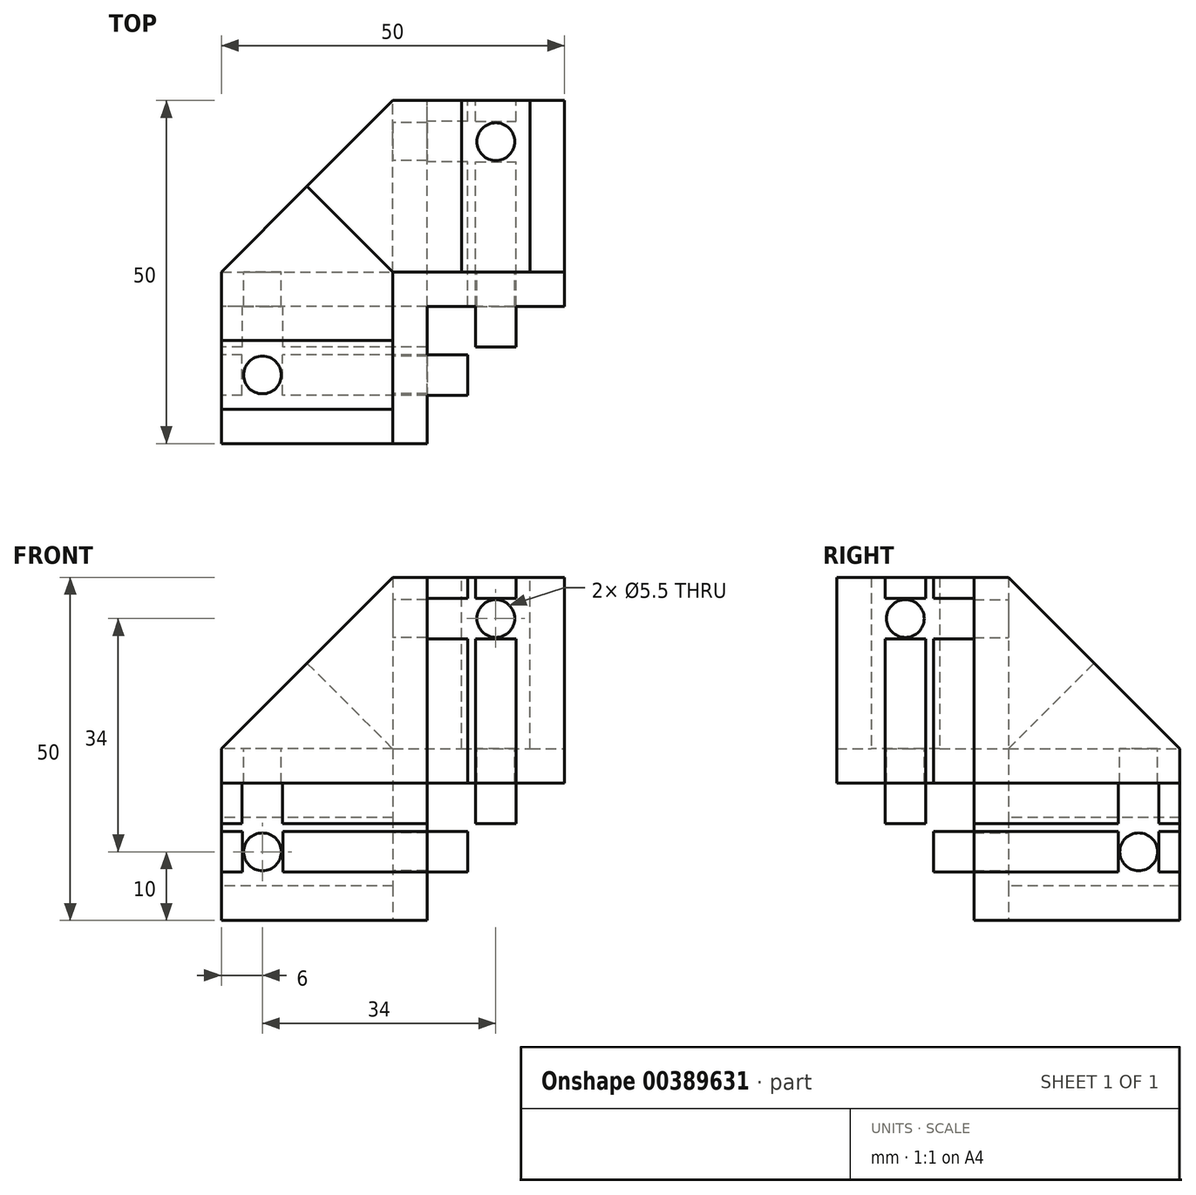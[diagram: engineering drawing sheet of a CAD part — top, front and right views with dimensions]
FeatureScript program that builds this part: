
annotation { "Feature Type Name" : "Feature", "Feature Type Description" : "" }
export const myFeature = defineFeature(function(context is Context, id is Id, definition is map)
    precondition{}
    {
        {
            var Q0;
            Q0=qCreatedBy(makeId("Top.planeOp"),FACE);
            var sketch = newSketch(context, id + "F0", { "sketchPlane" : qUnion([Q0])});
            skLineSegment(sketch, "E0", {"start": v(25, 25) * mm, "end": v(0, 25) * mm});
            skLineSegment(sketch, "E1", {"start": v(0, 25) * mm, "end": v(-25, 0) * mm});
            skLineSegment(sketch, "E2", {"start": v(-25, 0) * mm, "end": v(-25, -25) * mm});
            skLineSegment(sketch, "E3", {"start": v(-25, -25) * mm, "end": v(5, -25) * mm});
            skLineSegment(sketch, "E4", {"start": v(5, -25) * mm, "end": v(5, -5) * mm});
            skLineSegment(sketch, "E5", {"start": v(5, -5) * mm, "end": v(25, -5) * mm});
            skLineSegment(sketch, "E6", {"start": v(25, 25) * mm, "end": v(25, -5) * mm});
            skLineSegment(sketch, "E7", {"start": v(5, -5) * mm, "end": v(-25, -5) * mm});
            skLineSegment(sketch, "E8", {"start": v(5, -5) * mm, "end": v(5, 25) * mm});
            skSolve(sketch);
        }
        {
            var Q0;
            Q0=qSketchRegion(id+"F0",true);
            extrude(context, id + "F1", {"entities" : qUnion([Q0]), "depth" : 50 * mm});
        }
        {
            var Q0;
            {var subQ0=sQuery(id+"F0.wireOp",EDGE,"E3");Q0=makeQuery(id+"F0.imprint","IMPRINT",FACE,{"disambiguationData":[TD([[makeQuery(id+"F0.imprint","IMPRINT",EDGE,{"derivedFrom":subQ0}),1.0]])]});}
            var Q1;
            Q1=makeQuery(id+"F0.imprint","IMPRINT",FACE,{"disambiguationData":[TD([[makeQuery(id+"F0.imprint","IMPRINT",EDGE,{"derivedFrom":sQuery(id+"F0.wireOp",EDGE,"E5")}),1.0]])]});
            extrude(context, id + "F2", {"entities" : qUnion([Q0, Q1]), "operationType" : NewBodyOperationType.REMOVE, "depth" : 20 * mm});
        }
        {
            var Q0;
            Q0=makeQuery(id+"F1.opExtrude","CAP_EDGE",EDGE,{"disambiguationData":[OSD([sQuery(id+"F0.wireOp",EDGE,"E0")])],"isStart":false});
            var Q1;
            Q1=makeQuery(id+"F1.opExtrude","CAP_EDGE",EDGE,{"disambiguationData":[OSD([sQuery(id+"F0.wireOp",EDGE,"E2")])],"isStart":false});
            chamfer(context, id + "F3", {"entities" : qUnion([Q0, Q1]), "width" : 25 * mm, "tangentPropagation" : true});
        }
        {
            var Q0;
            Q0=makeQuery(id+"F1.opExtrude","SWEPT_FACE",FACE,{"disambiguationData":[OSD([sQuery(id+"F0.wireOp",EDGE,"E6")])]});
            cPlane(context, id + "F4", {"entities" : qUnion([Q0]), "cplaneType" : CPlaneType.OFFSET, "offset" : 5 * mm, "oppositeDirection" : true, "width" : 150 * mm, "height" : 150 * mm});
        }
        {
            var Q0;
            Q0=qCreatedBy(id+"F4.planeOp",FACE);
            var sketch = newSketch(context, id + "F5", { "sketchPlane" : qUnion([Q0])});
            skLineSegment(sketch, "E9.0", {"start": v(25, 25) * mm, "end": v(0, 50) * mm});
            skLineSegment(sketch, "E10", {"start": v(0, 50) * mm, "end": v(0, 25) * mm});
            skLineSegment(sketch, "E11", {"start": v(0, 25) * mm, "end": v(25, 25) * mm});
            skSolve(sketch);
        }
        {
            var Q0;
            Q0=qSketchRegion(id+"F5",true);
            extrude(context, id + "F6", {"entities" : qUnion([Q0]), "operationType" : NewBodyOperationType.REMOVE, "oppositeDirection" : true, "depth" : 10 * mm});
        }
        {
            var Q0;
            Q0=makeQuery(id+"F1.opExtrude","SWEPT_FACE",FACE,{"disambiguationData":[OSD([sQuery(id+"F0.wireOp",EDGE,"E3")])]});
            cPlane(context, id + "F7", {"entities" : qUnion([Q0]), "cplaneType" : CPlaneType.OFFSET, "offset" : 5 * mm, "oppositeDirection" : true, "width" : 150 * mm, "height" : 150 * mm});
        }
        {
            var Q0;
            Q0=qCreatedBy(id+"F7.planeOp",FACE);
            var sketch = newSketch(context, id + "F8", { "sketchPlane" : qUnion([Q0])});
            skLineSegment(sketch, "E12.0", {"start": v(0, 50) * mm, "end": v(-25, 25) * mm});
            skLineSegment(sketch, "E13", {"start": v(0, 50) * mm, "end": v(0, 25) * mm});
            skLineSegment(sketch, "E14", {"start": v(0, 25) * mm, "end": v(-25, 25) * mm});
            skSolve(sketch);
        }
        {
            var Q0;
            Q0=qSketchRegion(id+"F8",true);
            extrude(context, id + "F9", {"entities" : qUnion([Q0]), "operationType" : NewBodyOperationType.REMOVE, "oppositeDirection" : true, "depth" : 10 * mm});
        }
        {
            var Q0;
            {var subQ2=sQuery(id+"F0.wireOp",EDGE,"E1");Q0=makeQuery(id+"F0.imprint","IMPRINT",FACE,{"disambiguationData":[TD([[makeQuery(id+"F0.imprint","IMPRINT",EDGE,{"derivedFrom":subQ2}),1.0]])]});}
            cPlane(context, id + "F10", {"entities" : qUnion([Q0]), "cplaneType" : CPlaneType.OFFSET, "offset" : 5 * mm, "width" : 150 * mm, "height" : 150 * mm});
        }
        {
            var Q0;
            Q0=qCreatedBy(id+"F10.planeOp",FACE);
            var sketch = newSketch(context, id + "F11", { "sketchPlane" : qUnion([Q0])});
            skLineSegment(sketch, "E15.0", {"start": v(0, 25) * mm, "end": v(-25, 0) * mm});
            skLineSegment(sketch, "E16", {"start": v(-25, 0) * mm, "end": v(0, 0) * mm});
            skLineSegment(sketch, "E17", {"start": v(0, 0) * mm, "end": v(0, 25) * mm});
            skSolve(sketch);
        }
        {
            var Q0;
            Q0=qSketchRegion(id+"F11",true);
            extrude(context, id + "F12", {"entities" : qUnion([Q0]), "operationType" : NewBodyOperationType.REMOVE, "depth" : 10 * mm});
        }
        {
            var Q0;
            Q0=makeQuery(id+"F9.boolean.opBoolean","COPY",FACE,{"derivedFrom":makeQuery(id+"F9.opExtrude","SWEPT_FACE",FACE,{"disambiguationData":[OSD([sQuery(id+"F8.wireOp",EDGE,"E13")])]})});
            var sketch = newSketch(context, id + "F13", { "sketchPlane" : qUnion([Q0])});
            skCircle(sketch, "E18", {"center": v(15, 44) * mm, "radius": 2.75 * mm});
            skPoint(sketch, "E18.centerSnap0", {"position": v(15, 50) * mm});
            skSolve(sketch);
        }
        {
            var Q0;
            Q0=qSketchRegion(id+"F13",true);
            extrude(context, id + "F14", {"entities" : qUnion([Q0]), "operationType" : NewBodyOperationType.REMOVE, "oppositeDirection" : true, "depth" : 5 * mm});
        }
        {
            var Q0;
            Q0=makeQuery(id+"F9.boolean.opBoolean","COPY",FACE,{"derivedFrom":makeQuery(id+"F9.opExtrude","SWEPT_FACE",FACE,{"disambiguationData":[OSD([sQuery(id+"F8.wireOp",EDGE,"E14")])]})});
            var sketch = newSketch(context, id + "F15", { "sketchPlane" : qUnion([Q0])});
            skCircle(sketch, "E19", {"center": v(-19, -15) * mm, "radius": 2.75 * mm});
            skPoint(sketch, "E19.centerSnap0", {"position": v(-25, -15) * mm});
            skSolve(sketch);
        }
        {
            var Q0;
            Q0=qSketchRegion(id+"F15",true);
            extrude(context, id + "F16", {"entities" : qUnion([Q0]), "operationType" : NewBodyOperationType.REMOVE, "oppositeDirection" : true, "depth" : 5 * mm});
        }
        {
            var Q0;
            Q0=makeQuery(id+"F12.boolean.opBoolean","COPY",FACE,{"derivedFrom":makeQuery(id+"F12.opExtrude","SWEPT_FACE",FACE,{"disambiguationData":[OSD([sQuery(id+"F11.wireOp",EDGE,"E16")])]})});
            var sketch = newSketch(context, id + "F17", { "sketchPlane" : qUnion([Q0])});
            skCircle(sketch, "E20", {"center": v(19, 10) * mm, "radius": 2.75 * mm});
            skPoint(sketch, "E20.centerSnap0", {"position": v(25, 10) * mm});
            skSolve(sketch);
        }
        {
            var Q0;
            Q0=qSketchRegion(id+"F17",true);
            extrude(context, id + "F18", {"entities" : qUnion([Q0]), "operationType" : NewBodyOperationType.REMOVE, "oppositeDirection" : true, "depth" : 5 * mm});
        }
        {
            var Q0;
            Q0=makeQuery(id+"F12.boolean.opBoolean","COPY",FACE,{"derivedFrom":makeQuery(id+"F12.opExtrude","SWEPT_FACE",FACE,{"disambiguationData":[OSD([sQuery(id+"F11.wireOp",EDGE,"E17")])]})});
            var sketch = newSketch(context, id + "F19", { "sketchPlane" : qUnion([Q0])});
            skCircle(sketch, "E21", {"center": v(-19, 10) * mm, "radius": 2.75 * mm});
            skPoint(sketch, "E21.centerSnap0", {"position": v(-25, 10) * mm});
            skSolve(sketch);
        }
        {
            var Q0;
            Q0=qSketchRegion(id+"F19",true);
            extrude(context, id + "F20", {"entities" : qUnion([Q0]), "operationType" : NewBodyOperationType.REMOVE, "oppositeDirection" : true, "depth" : 5 * mm});
        }
        {
            var Q0;
            Q0=makeQuery(id+"F6.boolean.opBoolean","COPY",FACE,{"derivedFrom":makeQuery(id+"F6.opExtrude","SWEPT_FACE",FACE,{"disambiguationData":[OSD([sQuery(id+"F5.wireOp",EDGE,"E11")])]})});
            var sketch = newSketch(context, id + "F21", { "sketchPlane" : qUnion([Q0])});
            skCircle(sketch, "E22", {"center": v(15, 19) * mm, "radius": 2.75 * mm});
            skPoint(sketch, "E22.centerSnap0", {"position": v(15, 25) * mm});
            skSolve(sketch);
        }
        {
            var Q0;
            Q0=qSketchRegion(id+"F21",true);
            extrude(context, id + "F22", {"entities" : qUnion([Q0]), "operationType" : NewBodyOperationType.REMOVE, "oppositeDirection" : true, "depth" : 5 * mm});
        }
        {
            var Q0;
            Q0=makeQuery(id+"F6.boolean.opBoolean","COPY",FACE,{"derivedFrom":makeQuery(id+"F6.opExtrude","SWEPT_FACE",FACE,{"disambiguationData":[OSD([sQuery(id+"F5.wireOp",EDGE,"E10")])]})});
            var sketch = newSketch(context, id + "F23", { "sketchPlane" : qUnion([Q0])});
            skCircle(sketch, "E23", {"center": v(-15, 44) * mm, "radius": 2.75 * mm});
            skPoint(sketch, "E23.centerSnap0", {"position": v(-15, 50) * mm});
            skSolve(sketch);
        }
        {
            var Q0;
            Q0=qSketchRegion(id+"F23",true);
            extrude(context, id + "F24", {"entities" : qUnion([Q0]), "operationType" : NewBodyOperationType.REMOVE, "oppositeDirection" : true, "depth" : 5 * mm});
        }
        {
            var Q0;
            Q0=makeQuery(id+"F1.opExtrude","SWEPT_FACE",FACE,{"disambiguationData":[OSD([sQuery(id+"F0.wireOp",EDGE,"E5")])]});
            var sketch = newSketch(context, id + "F25", { "sketchPlane" : qUnion([Q0])});
            skLineSegment(sketch, "E24.bottom", {"start": v(12.05, 20) * mm, "end": v(17.95, 20) * mm});
            skLineSegment(sketch, "E24.top", {"start": v(12.05, 50) * mm, "end": v(17.95, 50) * mm});
            skLineSegment(sketch, "E24.left", {"start": v(12.05, 20) * mm, "end": v(12.05, 41.05) * mm});
            skLineSegment(sketch, "E24.right", {"start": v(17.95, 20) * mm, "end": v(17.95, 41.05) * mm});
            skLineSegment(sketch, "E25.bottom", {"start": v(12.05, 46.95) * mm, "end": v(17.95, 46.95) * mm});
            skLineSegment(sketch, "E25.top", {"start": v(12.05, 41.05) * mm, "end": v(17.95, 41.05) * mm});
            skLineSegment(sketch, "E26.trimOffspring", {"start": v(12.05, 46.95) * mm, "end": v(12.05, 50) * mm});
            skLineSegment(sketch, "E27.trimOffspring", {"start": v(17.95, 46.95) * mm, "end": v(17.95, 50) * mm});
            skPoint(sketch, "E28.0.center.orphan", {"position": v(15, 44) * mm});
            skSolve(sketch);
        }
        {
            var Q0;
            Q0=qSketchRegion(id+"F25",true);
            extrude(context, id + "F26", {"entities" : qUnion([Q0]), "operationType" : NewBodyOperationType.ADD, "depth" : 5.9 * mm});
        }
        {
            var Q0;
            Q0=makeQuery(id+"F2.boolean.opBoolean","MERGE",FACE,{"disambiguationData":[OD(0.0)],"derivedFrom":[makeQuery(id+"F1.opExtrude","SWEPT_FACE",FACE,{"disambiguationData":[OSD([sQuery(id+"F0.wireOp",EDGE,"E4")])]}),makeQuery(id+"F2.opExtrude","SWEPT_FACE",FACE,{"disambiguationData":[OSD([sQuery(id+"F0.wireOp",EDGE,"E8")])]})]});
            var sketch = newSketch(context, id + "F27", { "sketchPlane" : qUnion([Q0])});
            skLineSegment(sketch, "E29.bottom", {"start": v(-17.95, 50) * mm, "end": v(-12.05, 50) * mm});
            skLineSegment(sketch, "E29.top", {"start": v(-17.95, 20) * mm, "end": v(-12.05, 20) * mm});
            skLineSegment(sketch, "E30.trimOffspring", {"start": v(-17.95, 50) * mm, "end": v(-17.95, 46.96) * mm});
            skLineSegment(sketch, "E31.trimOffspring", {"start": v(-12.05, 50) * mm, "end": v(-12.05, 46.96) * mm});
            skLineSegment(sketch, "E32.bottom", {"start": v(-17.95, 46.96) * mm, "end": v(-12.05, 46.96) * mm});
            skLineSegment(sketch, "E32.top", {"start": v(-17.95, 41.06) * mm, "end": v(-12.05, 41.06) * mm});
            skLineSegment(sketch, "E33.trimOffspring", {"start": v(-12.05, 41.06) * mm, "end": v(-12.05, 20) * mm});
            skLineSegment(sketch, "E34.trimOffspring", {"start": v(-17.95, 41.06) * mm, "end": v(-17.95, 20) * mm});
            skPoint(sketch, "E35.0.center.orphan", {"position": v(-15, 44) * mm});
            skSolve(sketch);
        }
        {
            var Q0;
            Q0=qSketchRegion(id+"F27",true);
            var Q1;
            Q1=qConstructionFilter(qBodyType(qCreatedBy(id+"F27",EDGE),BodyType.WIRE),ConstructionObject.NO);
            extrude(context, id + "F28", {"entities" : qUnion([Q0]), "operationType" : NewBodyOperationType.ADD, "surfaceEntities" : qUnion([Q1]), "depth" : 5.9 * mm});
        }
        {
            var Q0;
            Q0=makeQuery(id+"F28.boolean.opBoolean","MERGE",FACE,{"derivedFrom":[makeQuery(id+"F2.boolean.opBoolean","COPY",FACE,{"derivedFrom":makeQuery(id+"F2.opExtrude","CAP_FACE",FACE,{"disambiguationData":[OSD([sQuery(id+"F0.wireOp",EDGE,"E2"),sQuery(id+"F0.wireOp",EDGE,"E3"),sQuery(id+"F0.wireOp",EDGE,"E4"),sQuery(id+"F0.wireOp",EDGE,"E7")])],"isStart":false})}),makeQuery(id+"F28.opExtrude","SWEPT_FACE",FACE,{"disambiguationData":[OSD([sQuery(id+"F27.wireOp",EDGE,"E29.top")])]})]});
            var sketch = newSketch(context, id + "F29", { "sketchPlane" : qUnion([Q0])});
            skLineSegment(sketch, "E36.bottom", {"start": v(10.9, 17.95) * mm, "end": v(-16.06, 17.95) * mm});
            skLineSegment(sketch, "E36.top", {"start": v(10.9, 12.05) * mm, "end": v(-16.06, 12.05) * mm});
            skLineSegment(sketch, "E36.left", {"start": v(10.9, 17.95) * mm, "end": v(10.9, 12.05) * mm});
            skLineSegment(sketch, "E36.right", {"start": v(-25, 17.95) * mm, "end": v(-25, 12.05) * mm});
            skLineSegment(sketch, "E37.left", {"start": v(-21.96, 17.95) * mm, "end": v(-21.96, 12.05) * mm});
            skLineSegment(sketch, "E37.right", {"start": v(-16.06, 17.95) * mm, "end": v(-16.06, 12.05) * mm});
            skLineSegment(sketch, "E38.trimOffspring", {"start": v(-21.96, 17.95) * mm, "end": v(-25, 17.95) * mm});
            skPoint(sketch, "E39.0.center.orphan", {"position": v(-19, 15) * mm});
            skLineSegment(sketch, "E40.trimOffspring", {"start": v(-21.96, 12.05) * mm, "end": v(-25, 12.05) * mm});
            skSolve(sketch);
        }
        {
            var Q0;
            Q0=qSketchRegion(id+"F29",true);
            extrude(context, id + "F30", {"entities" : qUnion([Q0]), "operationType" : NewBodyOperationType.ADD, "depth" : 5.9 * mm});
        }
        {
            var Q0;
            Q0=makeQuery(id+"F26.boolean.opBoolean","MERGE",FACE,{"derivedFrom":[makeQuery(id+"F2.boolean.opBoolean","COPY",FACE,{"derivedFrom":makeQuery(id+"F2.opExtrude","CAP_FACE",FACE,{"disambiguationData":[OSD([sQuery(id+"F0.wireOp",EDGE,"E0"),sQuery(id+"F0.wireOp",EDGE,"E5"),sQuery(id+"F0.wireOp",EDGE,"E6"),sQuery(id+"F0.wireOp",EDGE,"E8")])],"isStart":false})}),makeQuery(id+"F26.opExtrude","SWEPT_FACE",FACE,{"disambiguationData":[OSD([sQuery(id+"F25.wireOp",EDGE,"E24.bottom")])]})]});
            var sketch = newSketch(context, id + "F31", { "sketchPlane" : qUnion([Q0])});
            skLineSegment(sketch, "E41.bottom", {"start": v(12.05, 10.9) * mm, "end": v(17.95, 10.9) * mm});
            skLineSegment(sketch, "E41.top", {"start": v(12.05, -25) * mm, "end": v(17.95, -25) * mm});
            skLineSegment(sketch, "E41.left", {"start": v(12.05, 10.9) * mm, "end": v(12.05, -16.04) * mm});
            skLineSegment(sketch, "E41.right", {"start": v(17.95, 10.9) * mm, "end": v(17.95, -16.04) * mm});
            skLineSegment(sketch, "E42.bottom", {"start": v(12.05, -16.04) * mm, "end": v(17.95, -16.04) * mm});
            skLineSegment(sketch, "E42.top", {"start": v(12.05, -21.94) * mm, "end": v(17.95, -21.94) * mm});
            skLineSegment(sketch, "E43.trimOffspring", {"start": v(12.05, -21.94) * mm, "end": v(12.05, -25) * mm});
            skLineSegment(sketch, "E44.trimOffspring", {"start": v(17.95, -21.94) * mm, "end": v(17.95, -25) * mm});
            skPoint(sketch, "E45.0.center.orphan", {"position": v(15, -19) * mm});
            skSolve(sketch);
        }
        {
            var Q0;
            Q0=qSketchRegion(id+"F31",true);
            extrude(context, id + "F32", {"entities" : qUnion([Q0]), "operationType" : NewBodyOperationType.ADD, "depth" : 5.9 * mm});
        }
        {
            var Q0;
            Q0=makeQuery(id+"F2.boolean.opBoolean","MERGE",FACE,{"disambiguationData":[OD(1.0)],"derivedFrom":[makeQuery(id+"F1.opExtrude","SWEPT_FACE",FACE,{"disambiguationData":[OSD([sQuery(id+"F0.wireOp",EDGE,"E4")])]}),makeQuery(id+"F2.opExtrude","SWEPT_FACE",FACE,{"disambiguationData":[OSD([sQuery(id+"F0.wireOp",EDGE,"E8")])]})]});
            var sketch = newSketch(context, id + "F33", { "sketchPlane" : qUnion([Q0])});
            skLineSegment(sketch, "E46.bottom", {"start": v(-5, 12.95) * mm, "end": v(16.06, 12.95) * mm});
            skLineSegment(sketch, "E46.top", {"start": v(-5, 7.05) * mm, "end": v(16.06, 7.05) * mm});
            skLineSegment(sketch, "E46.left", {"start": v(-5, 12.95) * mm, "end": v(-5, 7.05) * mm});
            skLineSegment(sketch, "E46.right", {"start": v(25, 12.95) * mm, "end": v(25, 7.05) * mm});
            skLineSegment(sketch, "E47.left", {"start": v(21.96, 12.95) * mm, "end": v(21.96, 7.05) * mm});
            skLineSegment(sketch, "E47.right", {"start": v(16.06, 12.95) * mm, "end": v(16.06, 7.05) * mm});
            skLineSegment(sketch, "E48.trimOffspring", {"start": v(21.96, 12.95) * mm, "end": v(25, 12.95) * mm});
            skLineSegment(sketch, "E49.trimOffspring", {"start": v(21.96, 7.05) * mm, "end": v(25, 7.05) * mm});
            skPoint(sketch, "E50.0.center.orphan", {"position": v(19, 10) * mm});
            skSolve(sketch);
        }
        {
            var Q0;
            Q0=qSketchRegion(id+"F33",true);
            extrude(context, id + "F34", {"entities" : qUnion([Q0]), "operationType" : NewBodyOperationType.ADD, "depth" : 5.9 * mm});
        }
        {
            var Q0;
            Q0=makeQuery(id+"F34.boolean.opBoolean","MERGE",FACE,{"derivedFrom":[makeQuery(id+"F2.boolean.opBoolean","COPY",FACE,{"derivedFrom":makeQuery(id+"F2.opExtrude","SWEPT_FACE",FACE,{"disambiguationData":[OSD([sQuery(id+"F0.wireOp",EDGE,"E7")])]})}),makeQuery(id+"F34.opExtrude","SWEPT_FACE",FACE,{"disambiguationData":[OSD([sQuery(id+"F33.wireOp",EDGE,"E46.left")])]})]});
            var sketch = newSketch(context, id + "F35", { "sketchPlane" : qUnion([Q0])});
            skPoint(sketch, "E51.oppositeSnap0", {"position": v(7.95, 7.05) * mm});
            skLineSegment(sketch, "E51.bottom", {"start": v(10.9, 12.95) * mm, "end": v(-16.05, 12.95) * mm});
            skLineSegment(sketch, "E51.top", {"start": v(10.9, 7.05) * mm, "end": v(-16.05, 7.05) * mm});
            skLineSegment(sketch, "E51.left", {"start": v(10.9, 12.95) * mm, "end": v(10.9, 7.05) * mm});
            skLineSegment(sketch, "E51.right", {"start": v(-25, 12.95) * mm, "end": v(-25, 7.05) * mm});
            skLineSegment(sketch, "E52.left", {"start": v(-21.95, 12.95) * mm, "end": v(-21.95, 7.05) * mm});
            skLineSegment(sketch, "E52.right", {"start": v(-16.05, 12.95) * mm, "end": v(-16.05, 7.05) * mm});
            skLineSegment(sketch, "E53.trimOffspring", {"start": v(-21.95, 12.95) * mm, "end": v(-25, 12.95) * mm});
            skLineSegment(sketch, "E54.trimOffspring", {"start": v(-21.95, 7.05) * mm, "end": v(-25, 7.05) * mm});
            skPoint(sketch, "E55.0.center.orphan", {"position": v(-19, 10) * mm});
            skSolve(sketch);
        }
        {
            var Q0;
            Q0=qSketchRegion(id+"F35",true);
            extrude(context, id + "F36", {"entities" : qUnion([Q0]), "operationType" : NewBodyOperationType.ADD, "depth" : 5.9 * mm});
        }
        {
            var Q0;
            Q0=makeQuery(id+"F36.boolean.opBoolean","MERGE",FACE,{"derivedFrom":[makeQuery(id+"F34.opExtrude","SWEPT_FACE",FACE,{"disambiguationData":[OSD([sQuery(id+"F33.wireOp",EDGE,"E46.top")])]}),makeQuery(id+"F36.opExtrude","SWEPT_FACE",FACE,{"disambiguationData":[OSD([sQuery(id+"F35.wireOp",EDGE,"E51.top")])]})]});
            var sketch = newSketch(context, id + "F37", { "sketchPlane" : qUnion([Q0])});
            skLineSegment(sketch, "E56.bottom", {"start": v(5, 5) * mm, "end": v(10.9, 5) * mm});
            skLineSegment(sketch, "E56.top", {"start": v(5, 10.9) * mm, "end": v(10.9, 10.9) * mm});
            skLineSegment(sketch, "E56.left", {"start": v(5, 5) * mm, "end": v(5, 10.9) * mm});
            skLineSegment(sketch, "E56.right", {"start": v(10.9, 5) * mm, "end": v(10.9, 10.9) * mm});
            skSolve(sketch);
        }
        {
            var Q0;
            Q0=qSketchRegion(id+"F37",true);
            extrude(context, id + "F38", {"entities" : qUnion([Q0]), "operationType" : NewBodyOperationType.REMOVE, "oppositeDirection" : true, "depth" : 5.9 * mm});
        }
        {
            var Q0;
            Q0=makeQuery(id+"F30.opExtrude","CAP_FACE",FACE,{"disambiguationData":[OSD([sQuery(id+"F29.wireOp",EDGE,"E36.bottom"),sQuery(id+"F29.wireOp",EDGE,"E36.top"),sQuery(id+"F29.wireOp",EDGE,"E36.left"),sQuery(id+"F29.wireOp",EDGE,"uJzoyV8y-MDC7-HHXk-vQcc-9VhEeurIVrdR.right")])],"isStart":false});
            var sketch = newSketch(context, id + "F39", { "sketchPlane" : qUnion([Q0])});
            skLineSegment(sketch, "E57.bottom", {"start": v(10.9, 17.95) * mm, "end": v(5, 17.95) * mm});
            skLineSegment(sketch, "E57.top", {"start": v(10.9, 12.05) * mm, "end": v(5, 12.05) * mm});
            skLineSegment(sketch, "E57.left", {"start": v(10.9, 17.95) * mm, "end": v(10.9, 12.05) * mm});
            skLineSegment(sketch, "E57.right", {"start": v(5, 17.95) * mm, "end": v(5, 12.05) * mm});
            skSolve(sketch);
        }
        {
            var Q0;
            Q0=qSketchRegion(id+"F39",true);
            extrude(context, id + "F40", {"entities" : qUnion([Q0]), "operationType" : NewBodyOperationType.REMOVE, "oppositeDirection" : true, "depth" : 5.9 * mm});
        }
        {
            var Q0;
            Q0=makeQuery(id+"F32.opExtrude","CAP_FACE",FACE,{"disambiguationData":[OSD([sQuery(id+"F31.wireOp",EDGE,"E41.bottom"),sQuery(id+"F31.wireOp",EDGE,"E41.left"),sQuery(id+"F31.wireOp",EDGE,"E41.right"),sQuery(id+"F31.wireOp",EDGE,"XuwYO9kf-bFcl-q7Kr-sJp0-gLoZZdFn0bEj.top")])],"isStart":false});
            var sketch = newSketch(context, id + "F41", { "sketchPlane" : qUnion([Q0])});
            skLineSegment(sketch, "E58.bottom", {"start": v(12.05, 10.9) * mm, "end": v(17.95, 10.9) * mm});
            skLineSegment(sketch, "E58.top", {"start": v(12.05, 5) * mm, "end": v(17.95, 5) * mm});
            skLineSegment(sketch, "E58.left", {"start": v(12.05, 10.9) * mm, "end": v(12.05, 5) * mm});
            skLineSegment(sketch, "E58.right", {"start": v(17.95, 10.9) * mm, "end": v(17.95, 5) * mm});
            skSolve(sketch);
        }
        {
            var Q0;
            Q0=qSketchRegion(id+"F41",true);
            extrude(context, id + "F42", {"entities" : qUnion([Q0]), "operationType" : NewBodyOperationType.REMOVE, "oppositeDirection" : true, "depth" : 5.9 * mm});
        }
    });
